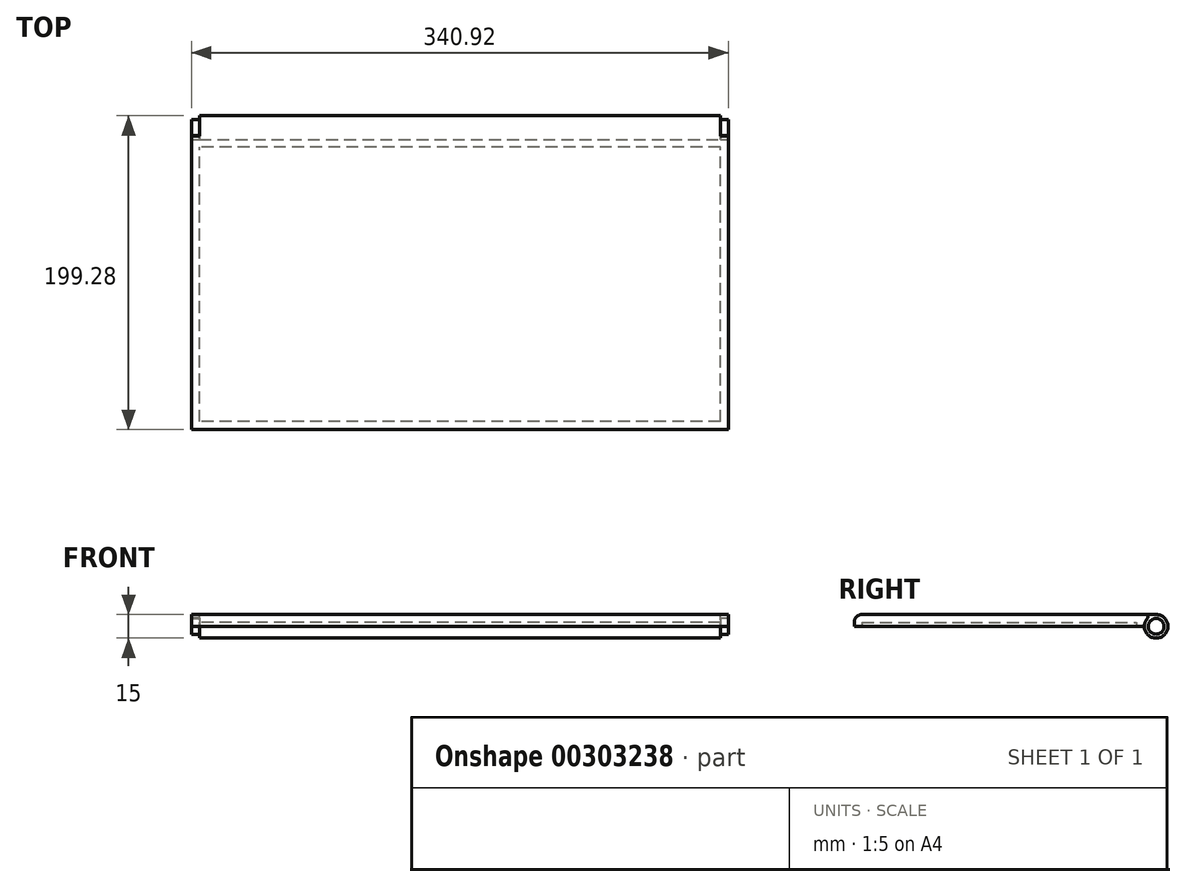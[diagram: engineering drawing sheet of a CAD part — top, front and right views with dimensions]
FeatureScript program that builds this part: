
annotation { "Feature Type Name" : "Feature", "Feature Type Description" : "" }
export const myFeature = defineFeature(function(context is Context, id is Id, definition is map)
    precondition{}
    {
        {
            var Q0;
            Q0=qCreatedBy(makeId("Top.planeOp"),FACE);
            var sketch = newSketch(context, id + "F0", { "sketchPlane" : qUnion([Q0])});
            skLineSegment(sketch, "E0.bottom", {"start": v(170.46, -95.89) * mm, "end": v(-170.46, -95.89) * mm});
            skLineSegment(sketch, "E0.top", {"start": v(170.46, 95.89) * mm, "end": v(-170.46, 95.89) * mm});
            skLineSegment(sketch, "E0.left", {"start": v(170.46, -95.89) * mm, "end": v(170.46, 95.89) * mm});
            skLineSegment(sketch, "E0.right", {"start": v(-170.46, -95.89) * mm, "end": v(-170.46, 95.89) * mm});
            skPoint(sketch, "E0.middle", {"position": v(0, 0) * mm});
            skSolve(sketch);
        }
        {
            var Q0;
            Q0 = qSketchRegion(id + "F0", true);
            extrude(context, id + "F1", {"entities" : qUnion([Q0]), "depth" : 7.5 * mm});
        }
        {
            var Q0;
            Q0=makeQuery(id+"F1.opExtrude","CAP_FACE",FACE,{"disambiguationData":[OSD([sQuery(id+"F0.wireOp",EDGE,"E0.bottom"),sQuery(id+"F0.wireOp",EDGE,"E0.top"),sQuery(id+"F0.wireOp",EDGE,"E0.left"),sQuery(id+"F0.wireOp",EDGE,"E0.right")])],"isStart":true});
            shell(context, id + "F2", {"entities" : qUnion([Q0]), "thickness" : 5 * mm});
        }
        {
            var Q0;
            Q0=makeQuery(id+"F1.opExtrude","SWEPT_FACE",FACE,{"disambiguationData":[OSD([sQuery(id+"F0.wireOp",EDGE,"E0.left")])]});
            var sketch = newSketch(context, id + "F3", { "sketchPlane" : qUnion([Q0])});
            skCircle(sketch, "E1", {"center": v(95.89, 0) * mm, "radius": 7.5 * mm});
            skCircle(sketch, "E2", {"center": v(95.89, 0) * mm, "radius": 5 * mm});
            skLineSegment(sketch, "E3", {"start": v(95.89, 7.5) * mm, "end": v(95.89, 5) * mm});
            skLineSegment(sketch, "E4", {"start": v(90.89, 0) * mm, "end": v(88.39, 0) * mm});
            skSolve(sketch);
        }
        {
            var Q0;
            Q0=makeQuery(id+"F2.opShell","OFFSET_FACE",FACE,{"disambiguationData":[OSD([sQuery(id+"F0.wireOp",EDGE,"E0.top")])]});
            extrude(context, id + "F4", {"entities" : qUnion([Q0]), "operationType" : NewBodyOperationType.ADD, "depth" : 2.5 * mm});
        }
        {
            var Q0;
            {var subQ1=sQuery(id+"F0.wireOp",EDGE,"E0.left");var subQ2=makeQuery(id+"F1.opExtrude","SWEPT_EDGE",EDGE,{"disambiguationData":[OSD([sQuery(id+"F0.wireOp",EDGE,"E0.top"),subQ1])]});var subQ4=makeQuery(id+"F1.opExtrude","CAP_EDGE",EDGE,{"disambiguationData":[OSD([subQ1])],"isStart":true});var subQ6=makeQuery(id+"F3.imprint","INTERSECT",VERTEX,{"derivedFrom":[subQ2,subQ4]});Q0=makeQuery(id+"F3.imprint","IMPRINT",FACE,{"disambiguationData":[TD([[makeQuery(id+"F3.imprint","IMPRINT",EDGE,{"disambiguationData":[TD([[subQ6,1.0]])],"derivedFrom":subQ4}),1.0]])]});}
            var Q1;
            Q1=makeQuery(id+"F1.opExtrude","SWEPT_FACE",FACE,{"disambiguationData":[OSD([sQuery(id+"F0.wireOp",EDGE,"E0.right")])]});
            extrude(context, id + "F5", {"entities" : qUnion([Q0]), "operationType" : NewBodyOperationType.REMOVE, "endBound" : BoundingType.UP_TO_SURFACE, "oppositeDirection" : true, "endBoundEntityFace" : qUnion([Q1]), "depth" : 25 * mm});
        }
        {
            var Q0;
            Q0=makeQuery(id+"F4.opExtrude","CAP_FACE",FACE,{"disambiguationData":[OSD([sQuery(id+"F0.wireOp",EDGE,"E0.top")])],"isStart":false});
            extrude(context, id + "F6", {"entities" : qUnion([Q0]), "operationType" : NewBodyOperationType.ADD, "depth" : 2.5 * mm});
        }
        {
            var Q0;
            {var subQ0=sQuery(id+"F3.wireOp",EDGE,"E3");Q0=makeQuery(id+"F3.imprint","IMPRINT",FACE,{"disambiguationData":[TD([[makeQuery(id+"F3.imprint","IMPRINT",EDGE,{"derivedFrom":subQ0}),1.0]])]});}
            var Q1;
            {var subQ1=sQuery(id+"F0.wireOp",EDGE,"E0.left");var subQ2=makeQuery(id+"F1.opExtrude","SWEPT_EDGE",EDGE,{"disambiguationData":[OSD([sQuery(id+"F0.wireOp",EDGE,"E0.top"),subQ1])]});var subQ4=makeQuery(id+"F1.opExtrude","CAP_EDGE",EDGE,{"disambiguationData":[OSD([subQ1])],"isStart":true});var subQ6=makeQuery(id+"F3.imprint","INTERSECT",VERTEX,{"derivedFrom":[subQ2,subQ4]});Q1=makeQuery(id+"F3.imprint","IMPRINT",FACE,{"disambiguationData":[TD([[makeQuery(id+"F3.imprint","IMPRINT",EDGE,{"disambiguationData":[TD([[subQ6,1.0]])],"derivedFrom":subQ4}),-1.0]])]});}
            var Q2;
            {var subQ1=sQuery(id+"F0.wireOp",EDGE,"E0.left");var subQ2=makeQuery(id+"F1.opExtrude","SWEPT_EDGE",EDGE,{"disambiguationData":[OSD([sQuery(id+"F0.wireOp",EDGE,"E0.top"),subQ1])]});var subQ4=makeQuery(id+"F1.opExtrude","CAP_EDGE",EDGE,{"disambiguationData":[OSD([subQ1])],"isStart":true});var subQ6=makeQuery(id+"F3.imprint","INTERSECT",VERTEX,{"derivedFrom":[subQ2,subQ4]});Q2=makeQuery(id+"F3.imprint","IMPRINT",FACE,{"disambiguationData":[TD([[makeQuery(id+"F3.imprint","IMPRINT",EDGE,{"disambiguationData":[TD([[subQ6,1.0]])],"derivedFrom":subQ4}),1.0]])]});}
            extrude(context, id + "F7", {"entities" : qUnion([Q0, Q1, Q2]), "operationType" : NewBodyOperationType.ADD, "oppositeDirection" : true, "depth" : 335.93 * mm, "hasSecondDirection" : true, "secondDirectionOppositeDirection" : true, "secondDirectionDepth" : 5 * mm});
        }
        {
            var Q0;
            {var subQ0=sQuery(id+"F3.wireOp",EDGE,"E3");Q0=makeQuery(id+"F3.imprint","IMPRINT",FACE,{"disambiguationData":[TD([[makeQuery(id+"F3.imprint","IMPRINT",EDGE,{"derivedFrom":subQ0}),-1.0]])]});}
            extrude(context, id + "F8", {"entities" : qUnion([Q0]), "operationType" : NewBodyOperationType.REMOVE, "oppositeDirection" : true, "depth" : 5 * mm});
        }
        {
            var Q0;
            {var subQ0=sQuery(id+"F3.wireOp",EDGE,"E3");Q0=makeQuery(id+"F3.imprint","IMPRINT",FACE,{"disambiguationData":[TD([[makeQuery(id+"F3.imprint","IMPRINT",EDGE,{"derivedFrom":subQ0}),-1.0]])]});}
            extrude(context, id + "F9", {"entities" : qUnion([Q0]), "operationType" : NewBodyOperationType.REMOVE, "oppositeDirection" : true, "depth" : 340.93 * mm, "hasSecondDirection" : true, "secondDirectionOppositeDirection" : true, "secondDirectionDepth" : 335.93 * mm});
        }
        {
            var Q0;
            Q0=makeQuery(id+"F6.opExtrude","CAP_FACE",FACE,{"disambiguationData":[OSD([sQuery(id+"F0.wireOp",EDGE,"E0.top")])],"isStart":false});
            extrude(context, id + "F10", {"entities" : qUnion([Q0]), "operationType" : NewBodyOperationType.ADD, "depth" : 2.5 * mm});
        }
        {
            var Q0;
            {var subQ0=sQuery(id+"F3.wireOp",EDGE,"E4");var subQ1=sQuery(id+"F3.wireOp",EDGE,"E3");var subQ2=sQuery(id+"F3.wireOp",EDGE,"E2");var subQ3=sQuery(id+"F3.wireOp",EDGE,"E1");Q0=makeQuery(id+"F9.boolean.opBoolean","MERGE",FACE,{"derivedFrom":[makeQuery(id+"F7.opExtrude","CAP_FACE",FACE,{"disambiguationData":[OSD([subQ3,subQ2,subQ1,subQ0])],"isStart":false}),makeQuery(id+"F9.opExtrude","CAP_FACE",FACE,{"disambiguationData":[OSD([subQ3,subQ2,subQ1,subQ0])],"isStart":true})]});}
            var sketch = newSketch(context, id + "F11", { "sketchPlane" : qUnion([Q0])});
            skCircle(sketch, "E5", {"center": v(-95.89, 0) * mm, "radius": 5 * mm});
            skSolve(sketch);
        }
        {
            var Q0;
            {var subQ0=sQuery(id+"F3.wireOp",EDGE,"E4");var subQ1=sQuery(id+"F3.wireOp",EDGE,"E3");var subQ2=sQuery(id+"F3.wireOp",EDGE,"E2");var subQ3=sQuery(id+"F3.wireOp",EDGE,"E1");Q0=makeQuery(id+"F8.boolean.opBoolean","MERGE",FACE,{"derivedFrom":[makeQuery(id+"F7.opExtrude","CAP_FACE",FACE,{"disambiguationData":[OSD([subQ3,subQ2,subQ1,subQ0])],"isStart":true}),makeQuery(id+"F8.opExtrude","CAP_FACE",FACE,{"disambiguationData":[OSD([subQ3,subQ2,subQ1,subQ0])],"isStart":false})]});}
            var sketch = newSketch(context, id + "F12", { "sketchPlane" : qUnion([Q0])});
            skCircle(sketch, "E6", {"center": v(95.89, 0) * mm, "radius": 5 * mm});
            skSolve(sketch);
        }
        {
            var Q0;
            Q0 = qSketchRegion(id + "F12", true);
            extrude(context, id + "F13", {"entities" : qUnion([Q0]), "operationType" : NewBodyOperationType.ADD, "depth" : 5 * mm});
        }
        {
            var Q0;
            Q0=makeQuery(id+"F11.imprint","IMPRINT",FACE,{"disambiguationData":[TD([[makeQuery(id+"F11.imprint","IMPRINT",EDGE,{"derivedFrom":sQuery(id+"F11.wireOp",EDGE,"E5")}),1.0]])]});
            extrude(context, id + "F14", {"entities" : qUnion([Q0]), "operationType" : NewBodyOperationType.ADD, "depth" : 5 * mm});
        }
        {
            var Q0;
            Q0=makeQuery(id+"F1.opExtrude","CAP_EDGE",EDGE,{"disambiguationData":[OSD([sQuery(id+"F0.wireOp",EDGE,"E0.bottom")])],"isStart":false});
            fillet(context, id + "F15", {"entities" : qUnion([Q0]), "radius" : 5 * mm, "tangentPropagation" : true, "allowEdgeOverflow" : false});
        }
        {
            var Q0;
            Q0=makeQuery(id+"F1.opExtrude","SWEPT_FACE",FACE,{"disambiguationData":[OSD([sQuery(id+"F0.wireOp",EDGE,"E0.left")])]});
            var sketch = newSketch(context, id + "F16", { "sketchPlane" : qUnion([Q0])});
            skLineSegment(sketch, "E7", {"start": v(90.58, 5.3) * mm, "end": v(90.58, 7.5) * mm});
            skLineSegment(sketch, "E8", {"start": v(90.58, 7.5) * mm, "end": v(95.89, 7.5) * mm});
            skLineSegment(sketch, "E9", {"start": v(95.89, 7.5) * mm, "end": v(90.58, 5.3) * mm});
            skSolve(sketch);
        }
        {
            var Q0;
            Q0 = qSketchRegion(id + "F16", true);
            extrude(context, id + "F17", {"entities" : qUnion([Q0]), "operationType" : NewBodyOperationType.REMOVE, "oppositeDirection" : true, "depth" : 5 * mm});
        }
        {
            var Q0;
            Q0=makeQuery(id+"F1.opExtrude","SWEPT_FACE",FACE,{"disambiguationData":[OSD([sQuery(id+"F0.wireOp",EDGE,"E0.right")])]});
            var sketch = newSketch(context, id + "F18", { "sketchPlane" : qUnion([Q0])});
            skLineSegment(sketch, "E10", {"start": v(-90.58, 5.3) * mm, "end": v(-90.58, 7.5) * mm});
            skLineSegment(sketch, "E11", {"start": v(-90.58, 7.5) * mm, "end": v(-95.89, 7.5) * mm});
            skLineSegment(sketch, "E12", {"start": v(-95.89, 7.5) * mm, "end": v(-90.58, 5.3) * mm});
            skSolve(sketch);
        }
        {
            var Q0;
            Q0 = qSketchRegion(id + "F18", true);
            extrude(context, id + "F19", {"entities" : qUnion([Q0]), "operationType" : NewBodyOperationType.REMOVE, "oppositeDirection" : true, "depth" : 5 * mm});
        }
        {
            var Q0;
            {var subQ0=sQuery(id+"F0.wireOp",EDGE,"E0.top");var subQ1=makeQuery(id+"F2.opShell","OFFSET_EDGE",EDGE,{"disambiguationData":[OSD([subQ0]),TDD([makeQuery(id+"F1.opExtrude","CAP_EDGE",EDGE,{"disambiguationData":[OSD([subQ0])],"isStart":true})])]});var subQ2=makeQuery(id+"F4.opExtrude","CAP_EDGE",EDGE,{"disambiguationData":[OSD([subQ0]),TDD([subQ1])],"isStart":false});Q0=makeQuery(id+"F10.boolean.opBoolean","MERGE",FACE,{"derivedFrom":[makeQuery(id+"F6.boolean.opBoolean","MERGE",FACE,{"derivedFrom":[makeQuery(id+"F4.boolean.opBoolean","MERGE",FACE,{"derivedFrom":[makeQuery(id+"F1.opExtrude","CAP_FACE",FACE,{"disambiguationData":[OSD([sQuery(id+"F0.wireOp",EDGE,"E0.bottom"),subQ0,sQuery(id+"F0.wireOp",EDGE,"E0.left"),sQuery(id+"F0.wireOp",EDGE,"E0.right")])],"isStart":true}),makeQuery(id+"F4.opExtrude","SWEPT_FACE",FACE,{"disambiguationData":[OSD([subQ0]),TDD([subQ1])]})]}),makeQuery(id+"F6.opExtrude","SWEPT_FACE",FACE,{"disambiguationData":[OSD([subQ0]),TDD([subQ2])]})]}),makeQuery(id+"F10.opExtrude","SWEPT_FACE",FACE,{"disambiguationData":[OSD([subQ0]),TDD([makeQuery(id+"F6.opExtrude","CAP_EDGE",EDGE,{"disambiguationData":[OSD([subQ0]),TDD([subQ2])],"isStart":false})])]})]});}
            var sketch = newSketch(context, id + "F20", { "sketchPlane" : qUnion([Q0])});
            skLineSegment(sketch, "E13.bottom", {"start": v(-165.46, 90.89) * mm, "end": v(165.46, 90.89) * mm});
            skLineSegment(sketch, "E13.top", {"start": v(-165.46, -83.39) * mm, "end": v(165.46, -83.39) * mm});
            skLineSegment(sketch, "E13.left", {"start": v(-165.46, 90.89) * mm, "end": v(-165.46, -83.39) * mm});
            skLineSegment(sketch, "E13.right", {"start": v(165.46, 90.89) * mm, "end": v(165.46, -83.39) * mm});
            skSolve(sketch);
        }
        {
            var Q0;
            Q0 = qSketchRegion(id + "F20", true);
            var Q1;
            Q1=makeQuery(id+"F2.opShell","OFFSET_FACE",FACE,{"disambiguationData":[OSD([sQuery(id+"F0.wireOp",EDGE,"E0.bottom"),sQuery(id+"F0.wireOp",EDGE,"E0.top"),sQuery(id+"F0.wireOp",EDGE,"E0.left"),sQuery(id+"F0.wireOp",EDGE,"E0.right")])]});
            extrude(context, id + "F21", {"entities" : qUnion([Q0]), "endBound" : BoundingType.UP_TO_SURFACE, "oppositeDirection" : true, "endBoundEntityFace" : qUnion([Q1]), "depth" : 25 * mm});
        }
    });
